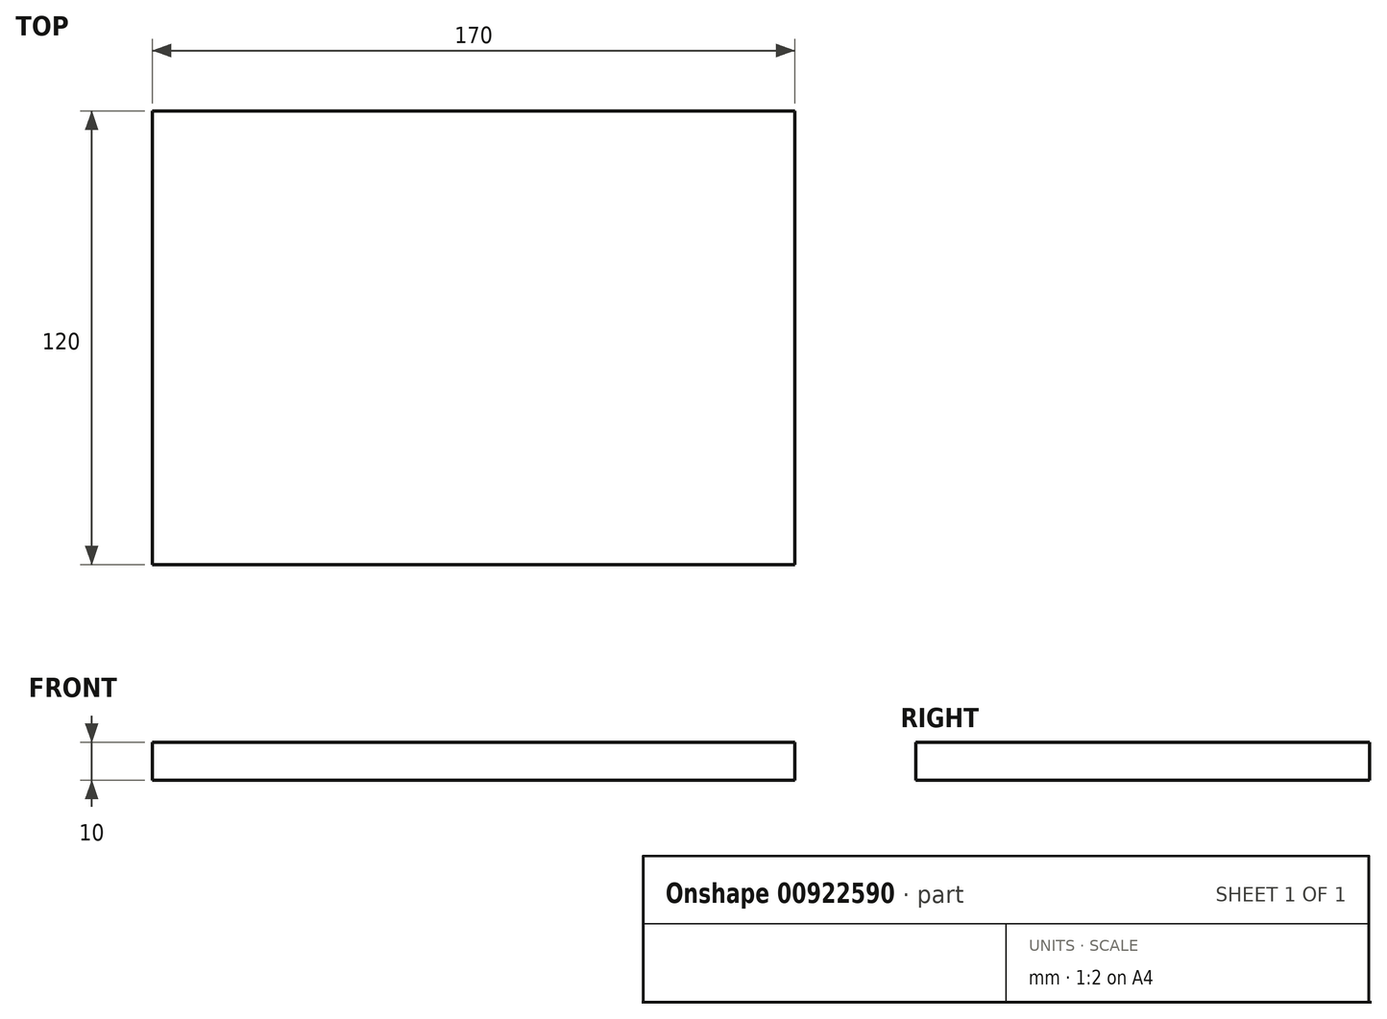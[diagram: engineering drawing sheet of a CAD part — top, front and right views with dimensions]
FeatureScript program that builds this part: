
annotation { "Feature Type Name" : "Feature", "Feature Type Description" : "" }
export const myFeature = defineFeature(function(context is Context, id is Id, definition is map)
    precondition{}
    {
        {
            var Q0;
            Q0=qCreatedBy(makeId("Top.planeOp"),FACE);
            var sketch = newSketch(context, id + "F0", { "sketchPlane" : qUnion([Q0])});
            skLineSegment(sketch, "E0.bottom", {"start": v(85, 60) * mm, "end": v(-85, 60) * mm});
            skLineSegment(sketch, "E0.top", {"start": v(85, -60) * mm, "end": v(-85, -60) * mm});
            skLineSegment(sketch, "E0.left", {"start": v(85, 60) * mm, "end": v(85, -60) * mm});
            skLineSegment(sketch, "E0.right", {"start": v(-85, 60) * mm, "end": v(-85, -60) * mm});
            skPoint(sketch, "E0.middle", {"position": v(0, 0) * mm});
            skSolve(sketch);
        }
        {
            var Q0;
            Q0 = qSketchRegion(id + "F0", true);
            extrude(context, id + "F1", {"entities" : qUnion([Q0]), "depth" : 10 * mm, "offsetDistance" : 25.4 * mm});
        }
    });
